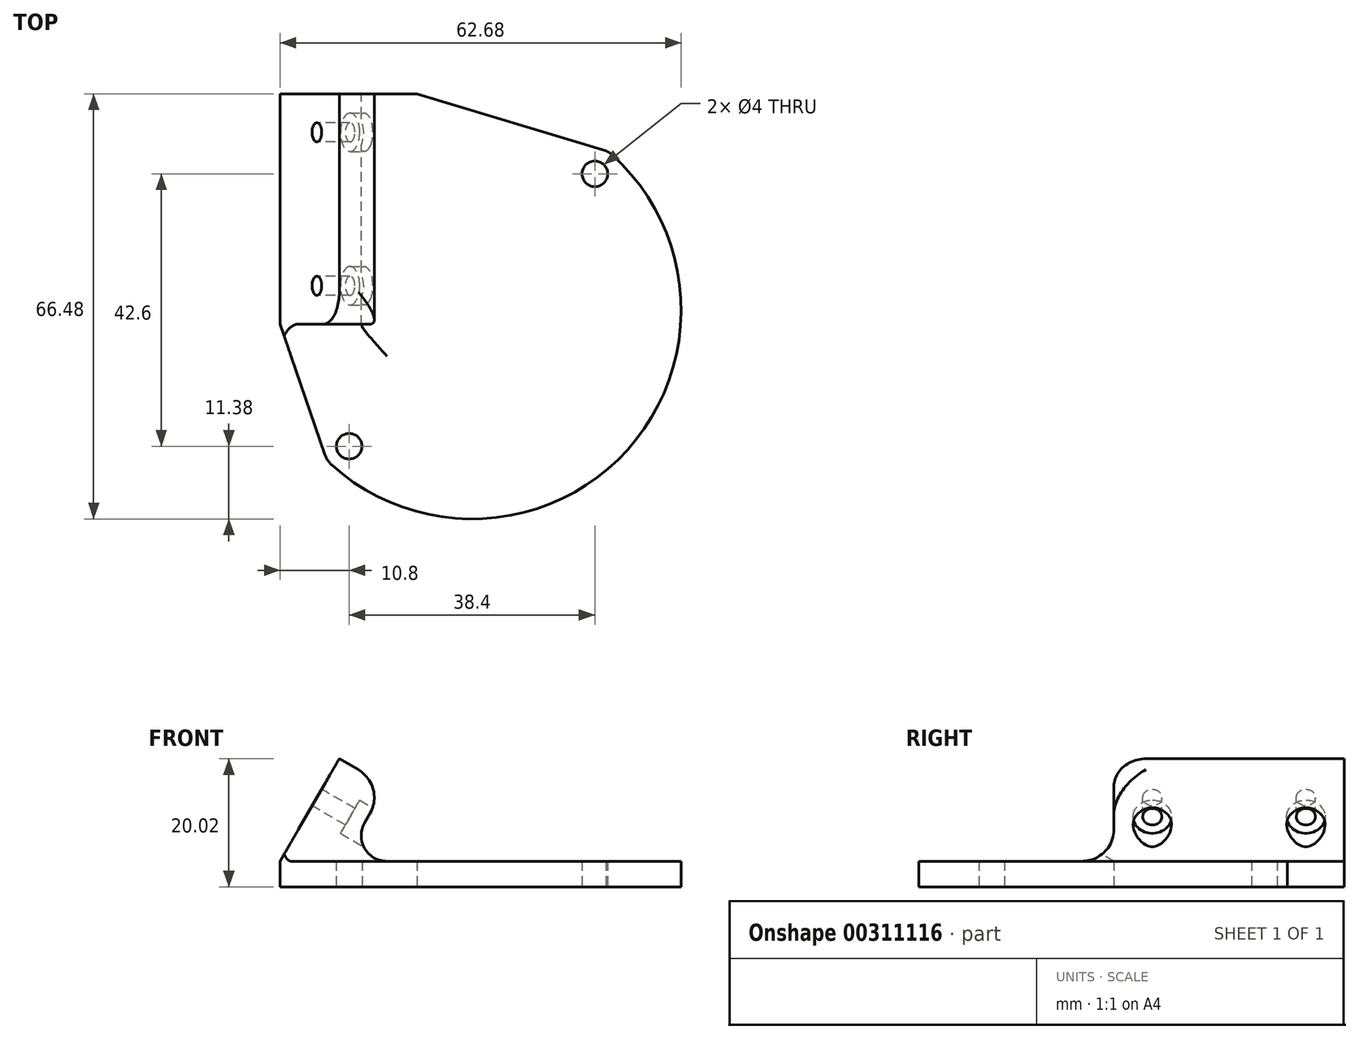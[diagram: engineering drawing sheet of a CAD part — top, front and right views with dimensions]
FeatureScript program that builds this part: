
annotation { "Feature Type Name" : "Feature", "Feature Type Description" : "" }
export const myFeature = defineFeature(function(context is Context, id is Id, definition is map)
    precondition{}
    {
        {
            var Q0;
            Q0=qCreatedBy(makeId("Top.planeOp"),FACE);
            var sketch = newSketch(context, id + "F0", { "sketchPlane" : qUnion([Q0])});
            skLineSegment(sketch, "E0", {"start": v(-21.88, -24.27) * mm, "end": v(21.88, 24.27) * mm, "construction": true});
            skCircle(sketch, "E1", {"center": v(-19.2, -21.3) * mm, "radius": 2 * mm});
            skCircle(sketch, "E2", {"center": v(19.2, 21.3) * mm, "radius": 2 * mm});
            skLineSegment(sketch, "E3", {"start": v(-50.42, -25.9) * mm, "end": v(40.64, -25.9) * mm, "construction": true});
            skLineSegment(sketch, "E4", {"start": v(25.1, 39.03) * mm, "end": v(25.1, -45.93) * mm, "construction": true});
            skLineSegment(sketch, "E5", {"start": v(-26, 39.03) * mm, "end": v(-26, 25.9) * mm, "construction": true});
            skLineSegment(sketch, "E6", {"start": v(-40.85, 25.9) * mm, "end": v(77.64, 25.9) * mm, "construction": true});
            skPoint(sketch, "E7", {"position": v(0, 0) * mm});
            skPoint(sketch, "E8", {"position": v(-26, 5.7) * mm});
            skLineSegment(sketch, "E9", {"start": v(-26, 25.9) * mm, "end": v(-26, -56.5) * mm, "construction": true});
            skLineSegment(sketch, "E10", {"start": v(-26, 5.7) * mm, "end": v(-26, 25.9) * mm, "construction": true});
            skLineSegment(sketch, "E11", {"start": v(-26, 15.8) * mm, "end": v(-30, 15.8) * mm, "construction": true});
            skPoint(sketch, "E11.endSnap0", {"position": v(-26, 15.8) * mm});
            skLineSegment(sketch, "E12", {"start": v(-28, -2.2) * mm, "end": v(-28, 33.8) * mm});
            skPoint(sketch, "E13.orphan", {"position": v(-28, 15.8) * mm});
            skPoint(sketch, "E14", {"position": v(16.52, 18.33) * mm});
            skPoint(sketch, "E15", {"position": v(-16.52, -18.33) * mm});
            skCircle(sketch, "E16", {"center": v(0, 0) * mm, "radius": 24.68 * mm, "construction": true});
            skArc(sketch, "E17", {"start": v(-21.88, -24.27) * mm, "mid": v(24.27, -21.88) * mm, "end": v(21.88, 24.27) * mm});
            skArc(sketch, "E18", {"start": v(-23.08, -22.25) * mm, "mid": v(-22.63, -23.35) * mm, "end": v(-21.88, -24.27) * mm});
            skArc(sketch, "E19", {"start": v(-21.88, -24.27) * mm, "mid": v(-15.77, -19.25) * mm, "end": v(-23.08, -22.25) * mm, "construction": true});
            skArc(sketch, "E20", {"start": v(19.9, 25.24) * mm, "mid": v(17.44, 17.7) * mm, "end": v(21.88, 24.27) * mm, "construction": true});
            skArc(sketch, "E21", {"start": v(21.88, 24.27) * mm, "mid": v(20.96, 24.9) * mm, "end": v(19.9, 25.24) * mm});
            skLineSegment(sketch, "E22", {"start": v(0, 28.8) * mm, "end": v(0, 20.18) * mm});
            skCircle(sketch, "E23.0", {"center": v(0, 0) * mm, "radius": 20.18 * mm});
            skPoint(sketch, "E24.orphan", {"position": v(0, 28.8) * mm});
            skLineSegment(sketch, "E25.bottom", {"start": v(-28, -2.2) * mm, "end": v(-30, -2.2) * mm});
            skLineSegment(sketch, "E25.left", {"start": v(-28, -2.2) * mm, "end": v(-28, 33.8) * mm, "construction": true});
            skLineSegment(sketch, "E25.right", {"start": v(-30, -2.2) * mm, "end": v(-30, 33.8) * mm});
            skLineSegment(sketch, "E26", {"start": v(-30, -2.2) * mm, "end": v(-22.98, -22.6) * mm});
            skLineSegment(sketch, "E27", {"start": v(-21.56, -2.2) * mm, "end": v(-21.56, 33.8) * mm});
            skPoint(sketch, "E27.endSnap0", {"position": v(-26, 32.46) * mm});
            skLineSegment(sketch, "E28", {"start": v(-28, -2.2) * mm, "end": v(-21.56, -2.2) * mm});
            skPoint(sketch, "E29.orphan", {"position": v(-21.56, 32.46) * mm});
            skLineSegment(sketch, "E30", {"start": v(-30, 33.8) * mm, "end": v(-21.56, 33.8) * mm});
            skLineSegment(sketch, "E31", {"start": v(-8.61, 33.8) * mm, "end": v(-21.56, 33.8) * mm});
            skLineSegment(sketch, "E32", {"start": v(-8.61, 33.8) * mm, "end": v(20.96, 24.9) * mm});
            skSolve(sketch);
        }
        {
            var Q0;
            Q0=makeQuery(id+"F0.imprint","IMPRINT",FACE,{"disambiguationData":[TD([[makeQuery(id+"F0.imprint","IMPRINT",EDGE,{"derivedFrom":sQuery(id+"F0.wireOp",EDGE,"E1")}),-1.0]])]});
            var Q1;
            {var subQ3=sQuery(id+"F0.wireOp",EDGE,"E22");Q1=makeQuery(id+"F0.imprint","IMPRINT",FACE,{"disambiguationData":[TD([[makeQuery(id+"F0.imprint","IMPRINT",EDGE,{"derivedFrom":subQ3}),-1.0]])]});}
            var Q2;
            {var subQ1=sQuery(id+"F0.wireOp",EDGE,"E12");Q2=makeQuery(id+"F0.imprint","IMPRINT",FACE,{"disambiguationData":[TD([[makeQuery(id+"F0.imprint","IMPRINT",EDGE,{"derivedFrom":subQ1}),-1.0]])]});}
            var Q3;
            Q3=makeQuery(id+"F0.imprint","IMPRINT",FACE,{"disambiguationData":[TD([[makeQuery(id+"F0.imprint","IMPRINT",EDGE,{"derivedFrom":sQuery(id+"F0.wireOp",EDGE,"E12")}),1.0]])]});
            var Q4;
            {var subQ0=sQuery(id+"F0.wireOp",EDGE,"wgmTAqz9-hJsv-3yCs-AEkT-I4p2Lc0dugmT");var subQ1=sQuery(id+"F0.wireOp",EDGE,"E23.0");var subQ3=makeQuery(id+"F0.imprint","INTERSECT",VERTEX,{"derivedFrom":[subQ1,subQ0]});Q4=makeQuery(id+"F0.imprint","IMPRINT",FACE,{"disambiguationData":[TD([[makeQuery(id+"F0.imprint","IMPRINT",EDGE,{"disambiguationData":[TD([[subQ3,-1.0]])],"derivedFrom":subQ1}),1.0]])]});}
            extrude(context, id + "F1", {"entities" : qUnion([Q0, Q1, Q2, Q3, Q4]), "depth" : 4 * mm});
        }
        {
            var Q0;
            {var subQ0=sQuery(id+"F0.wireOp",EDGE,"E12");Q0=makeQuery(id+"F0.imprint","IMPRINT",FACE,{"disambiguationData":[TD([[makeQuery(id+"F0.imprint","IMPRINT",EDGE,{"derivedFrom":subQ0}),-1.0]])]});}
            var Q1;
            {var subQ1=sQuery(id+"F0.wireOp",EDGE,"E12");Q1=makeQuery(id+"F0.imprint","IMPRINT",FACE,{"disambiguationData":[TD([[makeQuery(id+"F0.imprint","IMPRINT",EDGE,{"derivedFrom":subQ1}),1.0]])]});}
            extrude(context, id + "F2", {"entities" : qUnion([Q0, Q1]), "depth" : 18.5 * mm});
        }
        {
            var Q0;
            {var subQ0=sQuery(id+"F0.wireOp",EDGE,"E25.right");Q0=makeQuery(id+"F2.boolean.opBoolean","MERGE",FACE,{"derivedFrom":[makeQuery(id+"F1.opExtrude","SWEPT_FACE",FACE,{"disambiguationData":[OSD([subQ0])]}),makeQuery(id+"F2.opExtrude","SWEPT_FACE",FACE,{"disambiguationData":[OSD([subQ0])]})]});}
            var sketch = newSketch(context, id + "F3", { "sketchPlane" : qUnion([Q0])});
            skLineSegment(sketch, "E33", {"start": v(-31.8, 0) * mm, "end": v(2.2, 0) * mm, "construction": true});
            skLineSegment(sketch, "E34", {"start": v(2.2, 0) * mm, "end": v(-13.8, 0) * mm, "construction": true});
            skLineSegment(sketch, "E35", {"start": v(-27.8, 11.5) * mm, "end": v(-3.8, 11.5) * mm, "construction": true});
            skPoint(sketch, "E36", {"position": v(-15.8, 11.5) * mm});
            skCircle(sketch, "E37", {"center": v(-27.8, 11.5) * mm, "radius": 1.5 * mm});
            skCircle(sketch, "E38", {"center": v(-3.8, 11.5) * mm, "radius": 1.5 * mm});
            skSolve(sketch);
        }
        {
            var Q0;
            Q0=makeQuery(id+"F3.imprint","IMPRINT",FACE,{"disambiguationData":[TD([[makeQuery(id+"F3.imprint","IMPRINT",EDGE,{"derivedFrom":sQuery(id+"F3.wireOp",EDGE,"E37")}),1.0]])]});
            var Q1;
            Q1=makeQuery(id+"F3.imprint","IMPRINT",FACE,{"disambiguationData":[TD([[makeQuery(id+"F3.imprint","IMPRINT",EDGE,{"derivedFrom":sQuery(id+"F3.wireOp",EDGE,"E38")}),1.0]])]});
            extrude(context, id + "F4", {"entities" : qUnion([Q0, Q1]), "operationType" : NewBodyOperationType.REMOVE, "oppositeDirection" : true, "depth" : 25 * mm});
        }
        {
            var Q0;
            Q0=makeQuery(id+"F2.opExtrude","SWEPT_BODY",BODY,{"disambiguationData":[OSD([sQuery(id+"F0.wireOp",EDGE,"tb2RQikk-U185-NGek-2xLX-CrL1j7nIsQbI"),sQuery(id+"F0.wireOp",EDGE,"lIgoDh8n-qDbn-Urck-h8Jn-g8sGLXufOJtH"),sQuery(id+"F0.wireOp",EDGE,"E23.0"),sQuery(id+"F0.wireOp",EDGE,"wgmTAqz9-hJsv-3yCs-AEkT-I4p2Lc0dugmT"),sQuery(id+"F0.wireOp",EDGE,"E25.bottom"),sQuery(id+"F0.wireOp",EDGE,"E25.right"),sQuery(id+"F0.wireOp",EDGE,"FyWbMiXm-AazI-6GvB-5zjO-HR0zjYrNrkGQ")])]});
            var Q1;
            Q1=makeQuery(id+"F1.opExtrude","CAP_EDGE",EDGE,{"disambiguationData":[OSD([sQuery(id+"F0.wireOp",EDGE,"E25.right"),sQuery(id+"F0.wireOp",EDGE,"FyWbMiXm-AazI-6GvB-5zjO-HR0zjYrNrkGQ")])],"isStart":true});
            transform(context, id + "F5", {"entities" : qUnion([Q0]), "transformType" : TransformType.ROTATION, "transformAxis" : qUnion([Q1]), "angle" : 30 * degree, "makeCopy" : false});
        }
        {
            var Q0;
            Q0=makeQuery(id+"F2.opExtrude","SWEPT_BODY",BODY,{"disambiguationData":[OSD([sQuery(id+"F0.wireOp",EDGE,"tb2RQikk-U185-NGek-2xLX-CrL1j7nIsQbI"),sQuery(id+"F0.wireOp",EDGE,"lIgoDh8n-qDbn-Urck-h8Jn-g8sGLXufOJtH"),sQuery(id+"F0.wireOp",EDGE,"E23.0"),sQuery(id+"F0.wireOp",EDGE,"wgmTAqz9-hJsv-3yCs-AEkT-I4p2Lc0dugmT"),sQuery(id+"F0.wireOp",EDGE,"E25.bottom"),sQuery(id+"F0.wireOp",EDGE,"E25.right"),sQuery(id+"F0.wireOp",EDGE,"FyWbMiXm-AazI-6GvB-5zjO-HR0zjYrNrkGQ")])]});
            var Q1;
            Q1=qCreatedBy(makeId("Top.planeOp"),FACE);
            transform(context, id + "F6", {"entities" : qUnion([Q0]), "transformType" : TransformType.TRANSLATION_DISTANCE, "transformDirection" : qUnion([Q1]), "distance" : 4 * mm, "makeCopy" : false});
        }
        {
            var Q0;
            Q0=makeQuery(id+"F2.opExtrude","SWEPT_BODY",BODY,{"disambiguationData":[OSD([sQuery(id+"F0.wireOp",EDGE,"tb2RQikk-U185-NGek-2xLX-CrL1j7nIsQbI"),sQuery(id+"F0.wireOp",EDGE,"lIgoDh8n-qDbn-Urck-h8Jn-g8sGLXufOJtH"),sQuery(id+"F0.wireOp",EDGE,"E23.0"),sQuery(id+"F0.wireOp",EDGE,"wgmTAqz9-hJsv-3yCs-AEkT-I4p2Lc0dugmT"),sQuery(id+"F0.wireOp",EDGE,"E25.bottom"),sQuery(id+"F0.wireOp",EDGE,"E25.right"),sQuery(id+"F0.wireOp",EDGE,"FyWbMiXm-AazI-6GvB-5zjO-HR0zjYrNrkGQ")])]});
            var Q1;
            Q1=makeQuery(id+"F1.opExtrude","SWEPT_BODY",BODY,{"disambiguationData":[OSD([sQuery(id+"F0.wireOp",EDGE,"E1"),sQuery(id+"F0.wireOp",EDGE,"E2"),sQuery(id+"F0.wireOp",EDGE,"tb2RQikk-U185-NGek-2xLX-CrL1j7nIsQbI"),sQuery(id+"F0.wireOp",EDGE,"E17"),sQuery(id+"F0.wireOp",EDGE,"E18"),sQuery(id+"F0.wireOp",EDGE,"E21"),sQuery(id+"F0.wireOp",EDGE,"E23.0"),sQuery(id+"F0.wireOp",EDGE,"E25.right"),sQuery(id+"F0.wireOp",EDGE,"FyWbMiXm-AazI-6GvB-5zjO-HR0zjYrNrkGQ"),sQuery(id+"F0.wireOp",EDGE,"E26")])]});
            booleanBodies(context, id + "F7", {"operationType" : BooleanOperationType.UNION, "tools" : qUnion([Q0, Q1])});
        }
        {
            var Q0;
            {var subQ0=sQuery(id+"F0.wireOp",EDGE,"E22");Q0=makeQuery(id+"F0.imprint","IMPRINT",FACE,{"disambiguationData":[TD([[makeQuery(id+"F0.imprint","IMPRINT",EDGE,{"derivedFrom":subQ0}),-1.0]])]});}
            var Q1;
            Q1=makeQuery(id+"F0.imprint","IMPRINT",FACE,{"disambiguationData":[TD([[makeQuery(id+"F0.imprint","IMPRINT",EDGE,{"derivedFrom":sQuery(id+"F0.wireOp",EDGE,"E1")}),-1.0]])]});
            var Q2;
            {var subQ4=sQuery(id+"F0.wireOp",EDGE,"E12");Q2=makeQuery(id+"F0.imprint","IMPRINT",FACE,{"disambiguationData":[TD([[makeQuery(id+"F0.imprint","IMPRINT",EDGE,{"derivedFrom":subQ4}),-1.0]])]});}
            var Q3;
            {var subQ1=sQuery(id+"F0.wireOp",EDGE,"E12");Q3=makeQuery(id+"F0.imprint","IMPRINT",FACE,{"disambiguationData":[TD([[makeQuery(id+"F0.imprint","IMPRINT",EDGE,{"derivedFrom":subQ1}),1.0]])]});}
            extrude(context, id + "F8", {"entities" : qUnion([Q0, Q1, Q2, Q3]), "operationType" : NewBodyOperationType.REMOVE, "oppositeDirection" : true, "depth" : 2 * mm});
        }
        {
            var Q0;
            Q0=makeQuery(id+"F2.opExtrude","CAP_EDGE",EDGE,{"disambiguationData":[OSD([sQuery(id+"F0.wireOp",EDGE,"E27")])],"isStart":false});
            var Q1;
            Q1=makeQuery(id+"F2.opExtrude","CAP_EDGE",EDGE,{"disambiguationData":[OSD([sQuery(id+"F0.wireOp",EDGE,"E25.bottom"),sQuery(id+"F0.wireOp",EDGE,"E28")])],"isStart":false});
            var Q2;
            Q2=makeQuery(id+"F7.opBoolean","INTERSECT",EDGE,{"derivedFrom":[makeQuery(id+"F1.opExtrude","CAP_FACE",FACE,{"disambiguationData":[OSD([sQuery(id+"F0.wireOp",EDGE,"E1"),sQuery(id+"F0.wireOp",EDGE,"E2"),sQuery(id+"F0.wireOp",EDGE,"tb2RQikk-U185-NGek-2xLX-CrL1j7nIsQbI"),sQuery(id+"F0.wireOp",EDGE,"E17"),sQuery(id+"F0.wireOp",EDGE,"E18"),sQuery(id+"F0.wireOp",EDGE,"E21"),sQuery(id+"F0.wireOp",EDGE,"E23.0"),sQuery(id+"F0.wireOp",EDGE,"E25.right"),sQuery(id+"F0.wireOp",EDGE,"FyWbMiXm-AazI-6GvB-5zjO-HR0zjYrNrkGQ"),sQuery(id+"F0.wireOp",EDGE,"E26")])],"isStart":false}),makeQuery(id+"F2.opExtrude","SWEPT_FACE",FACE,{"disambiguationData":[OSD([sQuery(id+"F0.wireOp",EDGE,"E25.bottom"),sQuery(id+"F0.wireOp",EDGE,"E28")])]})]});
            var Q3;
            Q3=makeQuery(id+"F2.opExtrude","CAP_EDGE",EDGE,{"disambiguationData":[OSD([sQuery(id+"F0.wireOp",EDGE,"tb2RQikk-U185-NGek-2xLX-CrL1j7nIsQbI")])],"isStart":false});
            fillet(context, id + "F9", {"entities" : qUnion([Q0, Q1, Q2, Q3]), "radius" : 5 * mm, "tangentPropagation" : true, "allowEdgeOverflow" : false});
        }
        {
            var Q0;
            Q0=makeQuery(id+"F7.opBoolean","INTERSECT",EDGE,{"derivedFrom":[makeQuery(id+"F1.opExtrude","CAP_FACE",FACE,{"disambiguationData":[OSD([sQuery(id+"F0.wireOp",EDGE,"E1"),sQuery(id+"F0.wireOp",EDGE,"E2"),sQuery(id+"F0.wireOp",EDGE,"tb2RQikk-U185-NGek-2xLX-CrL1j7nIsQbI"),sQuery(id+"F0.wireOp",EDGE,"E17"),sQuery(id+"F0.wireOp",EDGE,"E18"),sQuery(id+"F0.wireOp",EDGE,"E21"),sQuery(id+"F0.wireOp",EDGE,"E23.0"),sQuery(id+"F0.wireOp",EDGE,"E25.right"),sQuery(id+"F0.wireOp",EDGE,"FyWbMiXm-AazI-6GvB-5zjO-HR0zjYrNrkGQ"),sQuery(id+"F0.wireOp",EDGE,"E26")])],"isStart":false}),makeQuery(id+"F2.opExtrude","SWEPT_FACE",FACE,{"disambiguationData":[OSD([sQuery(id+"F0.wireOp",EDGE,"E27")])]})]});
            fillet(context, id + "F10", {"entities" : qUnion([Q0]), "radius" : 4 * mm, "tangentPropagation" : true, "allowEdgeOverflow" : false});
        }
        {
            var Q0;
            Q0=makeQuery(id+"F2.opExtrude","SWEPT_FACE",FACE,{"disambiguationData":[OSD([sQuery(id+"F0.wireOp",EDGE,"E25.right")])]});
            cPlane(context, id + "F11", {"entities" : qUnion([Q0]), "cplaneType" : CPlaneType.OFFSET, "offset" : 9 * mm, "oppositeDirection" : true, "width" : 150 * mm, "height" : 150 * mm});
        }
        {
            var Q0;
            Q0=qCreatedBy(id+"F11.planeOp",FACE);
            var sketch = newSketch(context, id + "F12", { "sketchPlane" : qUnion([Q0])});
            skCircle(sketch, "E39.0", {"center": v(-27.8, -0.04) * mm, "radius": 1.5 * mm});
            skCircle(sketch, "E39.1", {"center": v(-3.8, -0.04) * mm, "radius": 1.5 * mm});
            skCircle(sketch, "E40", {"center": v(-3.8, -0.04) * mm, "radius": 3 * mm});
            skCircle(sketch, "E41", {"center": v(-27.8, -0.04) * mm, "radius": 3 * mm});
            skSolve(sketch);
        }
        {
            var Q0;
            Q0=makeQuery(id+"F12.imprint","IMPRINT",FACE,{"disambiguationData":[TD([[makeQuery(id+"F12.imprint","IMPRINT",EDGE,{"derivedFrom":sQuery(id+"F12.wireOp",EDGE,"E39.1")}),1.0]])]});
            var Q1;
            Q1=makeQuery(id+"F12.imprint","IMPRINT",FACE,{"disambiguationData":[TD([[makeQuery(id+"F12.imprint","IMPRINT",EDGE,{"derivedFrom":sQuery(id+"F12.wireOp",EDGE,"E39.0")}),1.0]])]});
            var Q2;
            Q2=makeQuery(id+"F12.imprint","IMPRINT",FACE,{"disambiguationData":[TD([[makeQuery(id+"F12.imprint","IMPRINT",EDGE,{"derivedFrom":sQuery(id+"F12.wireOp",EDGE,"E39.1")}),-1.0]])]});
            var Q3;
            Q3=makeQuery(id+"F12.imprint","IMPRINT",FACE,{"disambiguationData":[TD([[makeQuery(id+"F12.imprint","IMPRINT",EDGE,{"derivedFrom":sQuery(id+"F12.wireOp",EDGE,"E39.0")}),-1.0]])]});
            var Q4;
            Q4=sQuery(id+"F12.wireOp",EDGE,"E39.1");
            var Q5;
            Q5=sQuery(id+"F12.wireOp",EDGE,"E39.0");
            extrude(context, id + "F13", {"entities" : qUnion([Q0, Q1, Q2, Q3]), "operationType" : NewBodyOperationType.REMOVE, "surfaceEntities" : qUnion([Q4, Q5]), "endBound" : BoundingType.SYMMETRIC, "depth" : 6 * mm});
        }
    });
